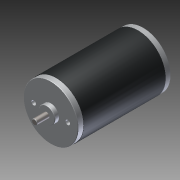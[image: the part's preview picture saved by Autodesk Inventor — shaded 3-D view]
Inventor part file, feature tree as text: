
AUTODESK INVENTOR PART (.ipt)
format: ipt  version: 2014 (Build 180170000, 170)  size: 123,392 bytes
history: native  units: in
note: dims shown in document units (in); Inventor stores cm internally (conversion verified against a paired STEP export)
features: chamfer x1, other x1, imported_body x1
ambient origin geometry x8: Origin, YZ Plane, XZ Plane, XY Plane, X Axis, Y Axis, Z Axis, Center Point
bodies: Body1 (feature_tree)
feature tree (3):
  chamfer  "Chamfer1"  [1 undecoded]
  other  "217-3351.ipt1"
  imported_body  "Base1"
note: 1 required parameter value undecoded (feature->parameter linkage not recoverable at this tier; creation-order binding heuristic only, values carry confidence <= 0.55)
